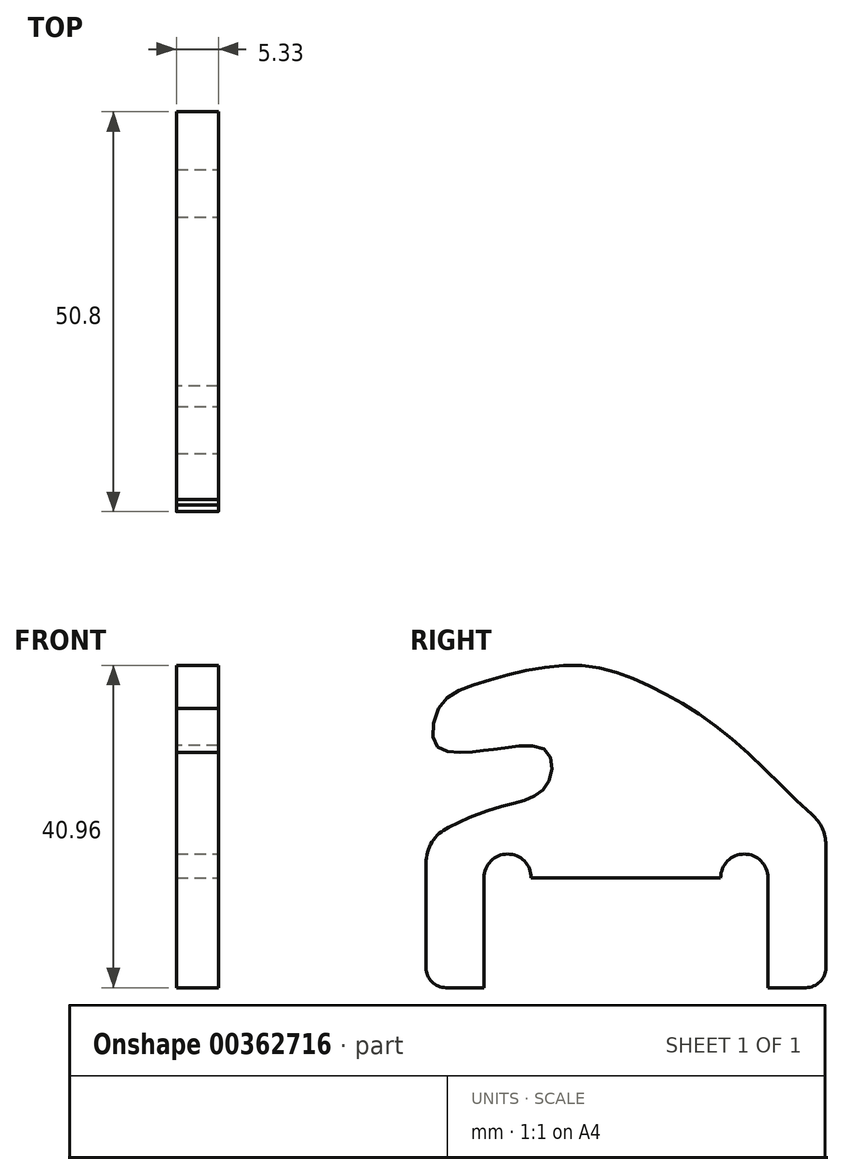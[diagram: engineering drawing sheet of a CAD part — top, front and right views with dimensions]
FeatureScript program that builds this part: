
annotation { "Feature Type Name" : "Feature", "Feature Type Description" : "" }
export const myFeature = defineFeature(function(context is Context, id is Id, definition is map)
    precondition{}
    {
        {
            var Q0;
            Q0=qCreatedBy(makeId("Right.planeOp"),FACE);
            var sketch = newSketch(context, id + "F0", { "sketchPlane" : qUnion([Q0])});
            skLineSegment(sketch, "E0.bottom", {"start": v(0, 11.43) * mm, "end": v(-50.8, 11.43) * mm, "construction": true});
            skLineSegment(sketch, "E0.top", {"start": v(0, 57.15) * mm, "end": v(-50.8, 57.15) * mm, "construction": true});
            skLineSegment(sketch, "E0.left", {"start": v(0, 11.43) * mm, "end": v(0, 57.15) * mm, "construction": true});
            skLineSegment(sketch, "E0.right", {"start": v(-50.8, 11.43) * mm, "end": v(-50.8, 57.15) * mm, "construction": true});
            skLineSegment(sketch, "E1", {"start": v(0, 57.15) * mm, "end": v(-50.8, 50.91) * mm, "construction": true});
            skLineSegment(sketch, "E2", {"start": v(-50.8, 40.68) * mm, "end": v(0, 46.91) * mm, "construction": true});
            skLineSegment(sketch, "E3", {"start": v(0, 36.68) * mm, "end": v(-50.8, 30.44) * mm, "construction": true});
            skLineSegment(sketch, "E4", {"start": v(0, 11.43) * mm, "end": v(0, 57.15) * mm});
            skLineSegment(sketch, "E5", {"start": v(-50.8, 11.43) * mm, "end": v(0, 11.43) * mm});
            skLineSegment(sketch, "E6", {"start": v(-50.8, 11.43) * mm, "end": v(-50.8, 30.44) * mm});
            skPoint(sketch, "E7.7.internal.snap0", {"position": v(-25.4, 43.8) * mm});
            skFitSpline(sketch, "E7", {"points": [v(0, 57.15) * mm, v(-32.05, 53.21) * mm, v(-41.7, 52.03) * mm, v(-48.3, 48.42) * mm, v(-49.49, 42.21) * mm, v(-44.96, 41.4) * mm, v(-41, 41.88) * mm, v(-35.52, 41.52) * mm, v(-35.33, 37.4) * mm, v(-38.4, 35.22) * mm, v(-45.21, 33.07) * mm, v(-54.09, 30.04) * mm], "startDerivative": vector(-81.22, -11.41) * mm, "endDerivative": vector(3.74, 50.03) * mm});
            skSolve(sketch);
        }
        {
            var Q0;
            Q0 = qSketchRegion(id + "F0", true);
            extrude(context, id + "F1", {"entities" : qUnion([Q0]), "depth" : 5.33 * mm});
        }
        {
            var Q0;
            Q0=makeQuery(id+"F1.opExtrude","CAP_FACE",FACE,{"disambiguationData":[OSD([sQuery(id+"F0.wireOp",EDGE,"E4"),sQuery(id+"F0.wireOp",EDGE,"kFnVzl44-yXa5-tqb7-hMSz-47kie5L9XpUL"),sQuery(id+"F0.wireOp",EDGE,"E5"),sQuery(id+"F0.wireOp",EDGE,"E6"),sQuery(id+"F0.wireOp",EDGE,"E7")])],"isStart":false});
            var sketch = newSketch(context, id + "F2", { "sketchPlane" : qUnion([Q0])});
            skFitSpline(sketch, "E8", {"points": [v(-43.17, 50.39) * mm, v(-31.9, 52.38) * mm, v(-22, 49.56) * mm, v(-11.24, 42.45) * mm, v(0, 32) * mm, v(7.05, 24.85) * mm, v(10.65, 11.43) * mm, v(5.78, 65.82) * mm, v(-60.34, 46.32) * mm, v(-52.5, 41.07) * mm, v(-49.22, 46.9) * mm, v(-43.17, 50.39) * mm]});
            skSolve(sketch);
        }
        {
            var Q0;
            Q0 = qSketchRegion(id + "F2", true);
            extrude(context, id + "F3", {"entities" : qUnion([Q0]), "operationType" : NewBodyOperationType.REMOVE, "endBound" : BoundingType.THROUGH_ALL, "oppositeDirection" : true, "depth" : 25.4 * mm});
        }
        {
            var Q0;
            Q0=makeQuery(id+"F1.opExtrude","SWEPT_EDGE",EDGE,{"disambiguationData":[OSD([sQuery(id+"F0.wireOp",EDGE,"E6"),sQuery(id+"F0.wireOp",EDGE,"E7")])]});
            var Q1;
            Q1=makeQuery(id+"F3.boolean.opBoolean","INTERSECT",EDGE,{"derivedFrom":[makeQuery(id+"F1.opExtrude","SWEPT_FACE",FACE,{"disambiguationData":[OSD([sQuery(id+"F0.wireOp",EDGE,"E4")])]}),makeQuery(id+"F3.opExtrude","SWEPT_FACE",FACE,{"disambiguationData":[OSD([sQuery(id+"F2.wireOp",EDGE,"E8")])]})]});
            fillet(context, id + "F4", {"entities" : qUnion([Q0, Q1]), "radius" : 5.08 * mm, "tangentPropagation" : true, "allowEdgeOverflow" : false});
        }
        {
            var Q0;
            Q0=makeQuery(id+"F1.opExtrude","SWEPT_EDGE",EDGE,{"disambiguationData":[OSD([sQuery(id+"F0.wireOp",EDGE,"E5"),sQuery(id+"F0.wireOp",EDGE,"E6")])]});
            var Q1;
            Q1=makeQuery(id+"F1.opExtrude","SWEPT_EDGE",EDGE,{"disambiguationData":[OSD([sQuery(id+"F0.wireOp",EDGE,"E4"),sQuery(id+"F0.wireOp",EDGE,"E5")])]});
            fillet(context, id + "F5", {"entities" : qUnion([Q0, Q1]), "radius" : 2.54 * mm, "tangentPropagation" : true, "allowEdgeOverflow" : false});
        }
        {
            var Q0;
            Q0=makeQuery(id+"F1.opExtrude","CAP_FACE",FACE,{"disambiguationData":[OSD([sQuery(id+"F0.wireOp",EDGE,"E4"),sQuery(id+"F0.wireOp",EDGE,"kFnVzl44-yXa5-tqb7-hMSz-47kie5L9XpUL"),sQuery(id+"F0.wireOp",EDGE,"E5"),sQuery(id+"F0.wireOp",EDGE,"99942b03-3897-4177-9158-4803bd176efe"),sQuery(id+"F0.wireOp",EDGE,"E6")])],"isStart":false});
            var sketch = newSketch(context, id + "F6", { "sketchPlane" : qUnion([Q0])});
            skLineSegment(sketch, "E9.bottom", {"start": v(-43.43, 11.43) * mm, "end": v(-7.37, 11.43) * mm});
            skLineSegment(sketch, "E9.top", {"start": v(-43.43, 25.4) * mm, "end": v(-7.37, 25.4) * mm});
            skLineSegment(sketch, "E9.left", {"start": v(-43.43, 11.43) * mm, "end": v(-43.43, 25.4) * mm});
            skLineSegment(sketch, "E9.right", {"start": v(-7.37, 11.43) * mm, "end": v(-7.37, 25.4) * mm});
            skPoint(sketch, "E10", {"position": v(-25.4, 11.43) * mm});
            skSolve(sketch);
        }
        {
            var Q0;
            Q0 = qSketchRegion(id + "F6", true);
            extrude(context, id + "F7", {"entities" : qUnion([Q0]), "operationType" : NewBodyOperationType.REMOVE, "oppositeDirection" : true, "depth" : 17.78 * mm});
        }
        {
            var Q0;
            Q0=makeQuery(id+"F1.opExtrude","CAP_FACE",FACE,{"disambiguationData":[OSD([sQuery(id+"F0.wireOp",EDGE,"E4"),sQuery(id+"F0.wireOp",EDGE,"kFnVzl44-yXa5-tqb7-hMSz-47kie5L9XpUL"),sQuery(id+"F0.wireOp",EDGE,"E5"),sQuery(id+"F0.wireOp",EDGE,"99942b03-3897-4177-9158-4803bd176efe"),sQuery(id+"F0.wireOp",EDGE,"E6")])],"isStart":false});
            var sketch = newSketch(context, id + "F8", { "sketchPlane" : qUnion([Q0])});
            skCircle(sketch, "E11", {"center": v(-10.37, 25.4) * mm, "radius": 3 * mm});
            skCircle(sketch, "E12", {"center": v(-40.43, 25.4) * mm, "radius": 3 * mm});
            skSolve(sketch);
        }
        {
            var Q0;
            Q0 = qSketchRegion(id + "F8", true);
            extrude(context, id + "F9", {"entities" : qUnion([Q0]), "operationType" : NewBodyOperationType.REMOVE, "oppositeDirection" : true, "depth" : 25.4 * mm});
        }
    });
